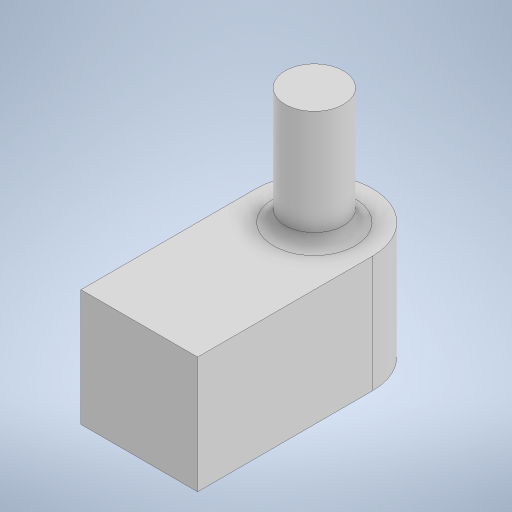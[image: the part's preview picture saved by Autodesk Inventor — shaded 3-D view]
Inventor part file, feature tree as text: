
AUTODESK INVENTOR PART (.ipt)
format: ipt  version: 2023 (Build 270158000, 158)  size: 228,864 bytes
history: native  units: mm
features: extrude x2, fillet x2, sketch x2
ambient origin geometry x8: Origin, YZ Plane, XZ Plane, XY Plane, X Axis, Y Axis, Z Axis, Center Point
bodies: Solido1 (feature_tree)
feature tree (6):
  extrude  "Estrusione1"  Depth=40.0mm
  extrude  "Estrusione2"  Depth=20.0mm
  fillet  "Raccordo1"  Radius=20.0mm
  fillet  "Raccordo2"  Radius=10.0mm
  sketch  "Schizzo1"
  sketch  "Schizzo2"
